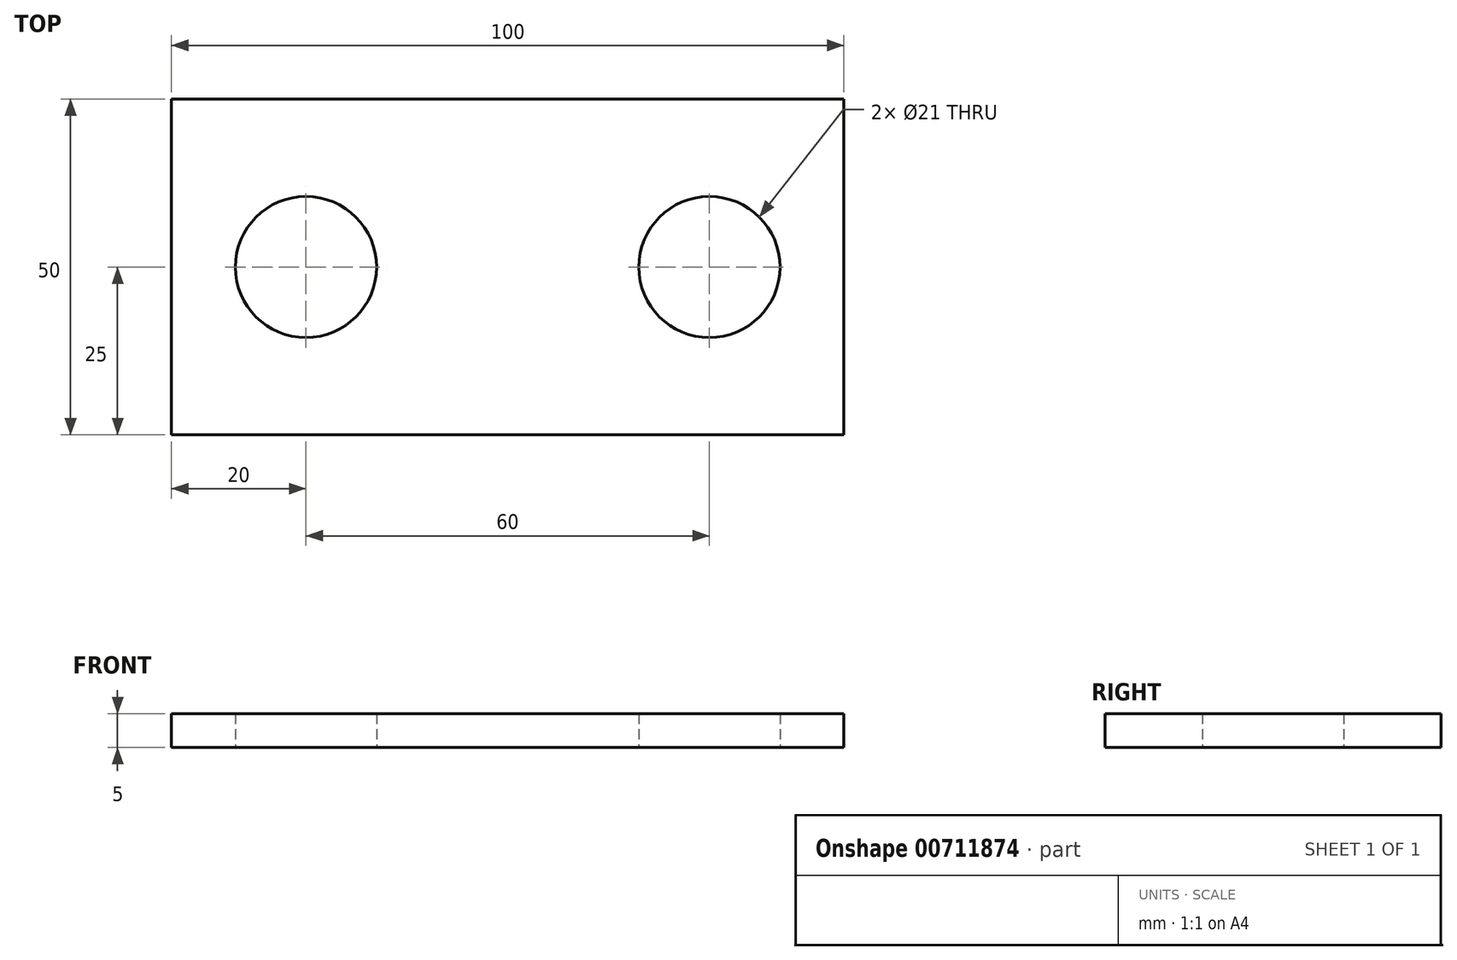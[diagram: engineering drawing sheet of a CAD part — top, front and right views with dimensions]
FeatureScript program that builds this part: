
annotation { "Feature Type Name" : "Feature", "Feature Type Description" : "" }
export const myFeature = defineFeature(function(context is Context, id is Id, definition is map)
    precondition{}
    {
        {
            var Q0;
            Q0=qCreatedBy(makeId("Top.planeOp"),FACE);
            var sketch = newSketch(context, id + "F0", { "sketchPlane" : qUnion([Q0])});
            skLineSegment(sketch, "E0.bottom", {"start": v(50, 25) * mm, "end": v(-50, 25) * mm});
            skLineSegment(sketch, "E0.top", {"start": v(50, -25) * mm, "end": v(-50, -25) * mm});
            skLineSegment(sketch, "E0.left", {"start": v(50, 25) * mm, "end": v(50, -25) * mm});
            skLineSegment(sketch, "E0.right", {"start": v(-50, 25) * mm, "end": v(-50, -25) * mm});
            skPoint(sketch, "E0.middle", {"position": v(0, 0) * mm});
            skCircle(sketch, "E1", {"center": v(-30, 0) * mm, "radius": 10.5 * mm});
            skCircle(sketch, "E2", {"center": v(30, 0) * mm, "radius": 10.5 * mm});
            skSolve(sketch);
        }
        {
            var Q0;
            Q0=makeQuery(id+"F0.imprint","IMPRINT",FACE,{"disambiguationData":[TD([[makeQuery(id+"F0.imprint","IMPRINT",EDGE,{"derivedFrom":sQuery(id+"F0.wireOp",EDGE,"E0.bottom")}),1.0]])]});
            extrude(context, id + "F1", {"entities" : qUnion([Q0]), "depth" : 5 * mm, "offsetDistance" : 25 * mm});
        }
    });
